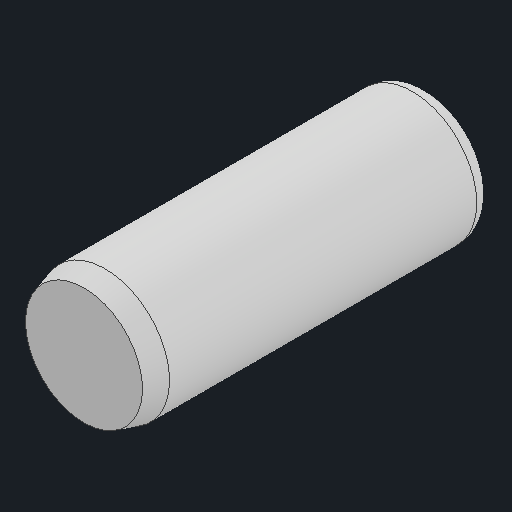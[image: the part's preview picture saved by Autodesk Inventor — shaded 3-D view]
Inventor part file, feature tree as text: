
AUTODESK INVENTOR PART (.ipt)
format: ipt  version: 2023 (Build 270158000, 158)  size: 108,544 bytes
history: native  units: in
note: dims shown in document units (in); Inventor stores cm internally (conversion verified against a paired STEP export)
features: revolve x1
ambient origin geometry x8: Origin, YZ Plane, XZ Plane, XY Plane, X Axis, Y Axis, Z Axis, Center Point
bodies: Solid1 (feature_tree)
feature tree (1):
  revolve  "Revolve1"  [1 undecoded]
note: 1 required parameter value undecoded (feature->parameter linkage not recoverable at this tier; creation-order binding heuristic only, values carry confidence <= 0.55)
